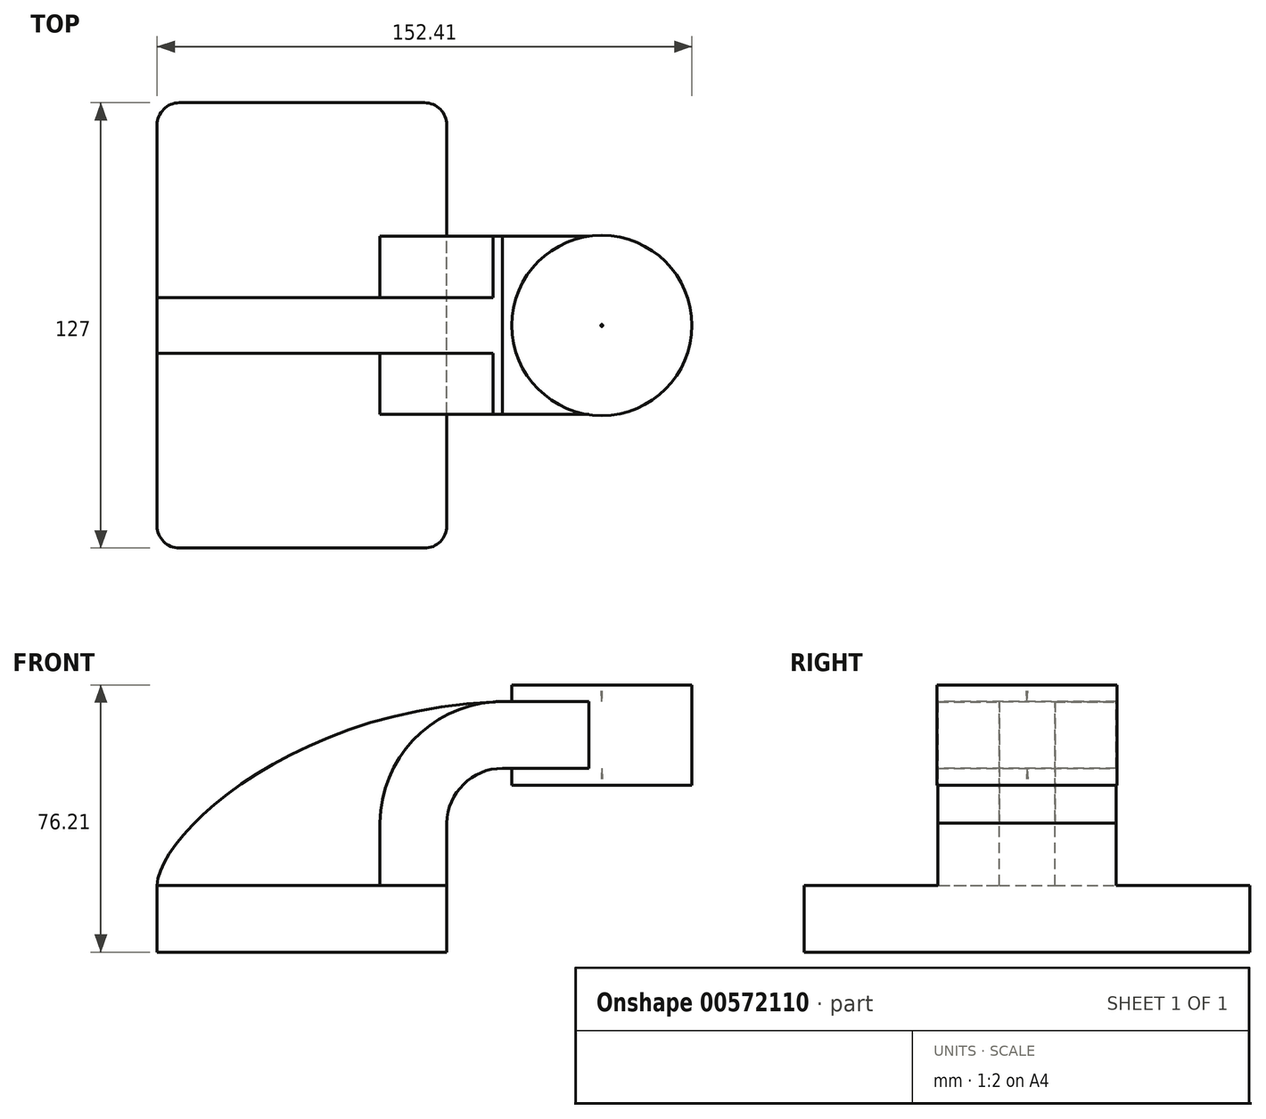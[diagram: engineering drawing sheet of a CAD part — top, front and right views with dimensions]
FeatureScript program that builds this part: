
annotation { "Feature Type Name" : "Feature", "Feature Type Description" : "" }
export const myFeature = defineFeature(function(context is Context, id is Id, definition is map)
    precondition{}
    {
        {
            var Q0;
            Q0=qCreatedBy(makeId("Front.planeOp"),FACE);
            var sketch = newSketch(context, id + "F0", { "sketchPlane" : qUnion([Q0])});
            skLineSegment(sketch, "E0.bottom", {"start": v(41.28, -9.52) * mm, "end": v(-41.28, -9.53) * mm});
            skLineSegment(sketch, "E0.top", {"start": v(41.28, 9.53) * mm, "end": v(-41.28, 9.53) * mm});
            skLineSegment(sketch, "E0.left", {"start": v(41.28, -9.52) * mm, "end": v(41.28, 9.53) * mm});
            skLineSegment(sketch, "E0.right", {"start": v(-41.28, -9.52) * mm, "end": v(-41.28, 9.53) * mm});
            skPoint(sketch, "E0.middle", {"position": v(0, 0) * mm});
            skLineSegment(sketch, "E1.bottom", {"start": v(60.32, 66.68) * mm, "end": v(111.12, 66.68) * mm});
            skLineSegment(sketch, "E1.top", {"start": v(60.33, 38.1) * mm, "end": v(111.12, 38.1) * mm});
            skLineSegment(sketch, "E1.left", {"start": v(60.32, 66.68) * mm, "end": v(60.32, 57.28) * mm});
            skLineSegment(sketch, "E1.right", {"start": v(111.12, 66.68) * mm, "end": v(111.12, 38.1) * mm});
            skLineSegment(sketch, "E2", {"start": v(41.28, 9.53) * mm, "end": v(41.28, 27.28) * mm});
            skArc(sketch, "E3", {"start": v(57.15, 42.88) * mm, "mid": v(46.02, 38.32) * mm, "end": v(41.28, 27.28) * mm});
            skPoint(sketch, "E4", {"position": v(85.73, 38.1) * mm});
            skLineSegment(sketch, "E5", {"start": v(60.32, 57.28) * mm, "end": v(60.33, 38.1) * mm});
            skLineSegment(sketch, "E6", {"start": v(57.15, 42.88) * mm, "end": v(85.45, 42.88) * mm});
            skLineSegment(sketch, "E7.0", {"start": v(57.15, 61.93) * mm, "end": v(85.45, 61.93) * mm});
            skArc(sketch, "E7.1", {"start": v(57.15, 61.93) * mm, "mid": v(32.6, 51.84) * mm, "end": v(22.22, 27.41) * mm});
            skLineSegment(sketch, "E7.2", {"start": v(22.22, 9.53) * mm, "end": v(22.22, 27.41) * mm});
            skFitSpline(sketch, "E8", {"points": [v(-41.28, 9.53) * mm, v(57.15, 61.93) * mm], "startDerivative": vector(1.22, 42.38) * mm, "endDerivative": vector(179.66, 5.46) * mm});
            skLineSegment(sketch, "E9", {"start": v(85.45, 61.93) * mm, "end": v(85.45, 42.88) * mm});
            skLineSegment(sketch, "E10", {"start": v(85.72, 66.68) * mm, "end": v(85.45, 61.93) * mm});
            skLineSegment(sketch, "E11", {"start": v(85.45, 42.88) * mm, "end": v(85.73, 38.1) * mm});
            skSolve(sketch);
        }
        {
            var Q0;
            Q0=makeQuery(id+"F0.imprint","IMPRINT",FACE,{"disambiguationData":[TD([[makeQuery(id+"F0.imprint","IMPRINT",EDGE,{"derivedFrom":sQuery(id+"F0.wireOp",EDGE,"E0.bottom")}),-1.0]])]});
            extrude(context, id + "F1", {"entities" : qUnion([Q0]), "endBound" : BoundingType.SYMMETRIC, "depth" : 127 * mm, "offsetDistance" : 25.4 * mm});
        }
        {
            var Q0;
            {var subQ0=sQuery(id+"F0.wireOp",EDGE,"E2");Q0=makeQuery(id+"F0.imprint","IMPRINT",FACE,{"disambiguationData":[TD([[makeQuery(id+"F0.imprint","IMPRINT",EDGE,{"derivedFrom":subQ0}),1.0]])]});}
            var Q1;
            {var subQ0=sQuery(id+"F0.wireOp",EDGE,"E9");Q1=makeQuery(id+"F0.imprint","IMPRINT",FACE,{"disambiguationData":[TD([[makeQuery(id+"F0.imprint","IMPRINT",EDGE,{"derivedFrom":subQ0}),-1.0]])]});}
            extrude(context, id + "F2", {"entities" : qUnion([Q0, Q1]), "operationType" : NewBodyOperationType.ADD, "endBound" : BoundingType.SYMMETRIC, "depth" : 50.8 * mm, "offsetDistance" : 25.4 * mm});
        }
        {
            var Q0;
            {var subQ3=sQuery(id+"F0.wireOp",EDGE,"E7.2");Q0=makeQuery(id+"F0.imprint","IMPRINT",FACE,{"disambiguationData":[TD([[makeQuery(id+"F0.imprint","IMPRINT",EDGE,{"derivedFrom":subQ3}),1.0]])]});}
            extrude(context, id + "F3", {"entities" : qUnion([Q0]), "operationType" : NewBodyOperationType.ADD, "endBound" : BoundingType.SYMMETRIC, "depth" : 15.88 * mm, "offsetDistance" : 25.4 * mm});
        }
        {
            var Q0;
            {var subQ0=sQuery(id+"F0.wireOp",EDGE,"E1.right");Q0=makeQuery(id+"F0.imprint","IMPRINT",FACE,{"disambiguationData":[TD([[makeQuery(id+"F0.imprint","IMPRINT",EDGE,{"derivedFrom":subQ0}),-1.0]])]});}
            var Q1;
            Q1=sQuery(id+"F0.wireOp",EDGE,"E9");
            revolve(context, id + "F4", {"operationType" : NewBodyOperationType.ADD, "entities" : qUnion([Q0]), "axis" : qUnion([Q1]), "revolveType" : RevolveType.FULL});
        }
        {
            var Q0;
            Q0=makeQuery(id+"F1.opExtrude","CAP_EDGE",EDGE,{"disambiguationData":[OSD([sQuery(id+"F0.wireOp",EDGE,"E0.left")])],"isStart":false});
            var Q1;
            Q1=makeQuery(id+"F1.opExtrude","CAP_EDGE",EDGE,{"disambiguationData":[OSD([sQuery(id+"F0.wireOp",EDGE,"E0.right")])],"isStart":false});
            var Q2;
            Q2=makeQuery(id+"F1.opExtrude","CAP_EDGE",EDGE,{"disambiguationData":[OSD([sQuery(id+"F0.wireOp",EDGE,"E0.left")])],"isStart":true});
            var Q3;
            Q3=makeQuery(id+"F1.opExtrude","CAP_EDGE",EDGE,{"disambiguationData":[OSD([sQuery(id+"F0.wireOp",EDGE,"E0.right")])],"isStart":true});
            fillet(context, id + "F5", {"entities" : qUnion([Q0, Q1, Q2, Q3]), "radius" : 6.35 * mm, "tangentPropagation" : true, "allowEdgeOverflow" : false});
        }
    });
